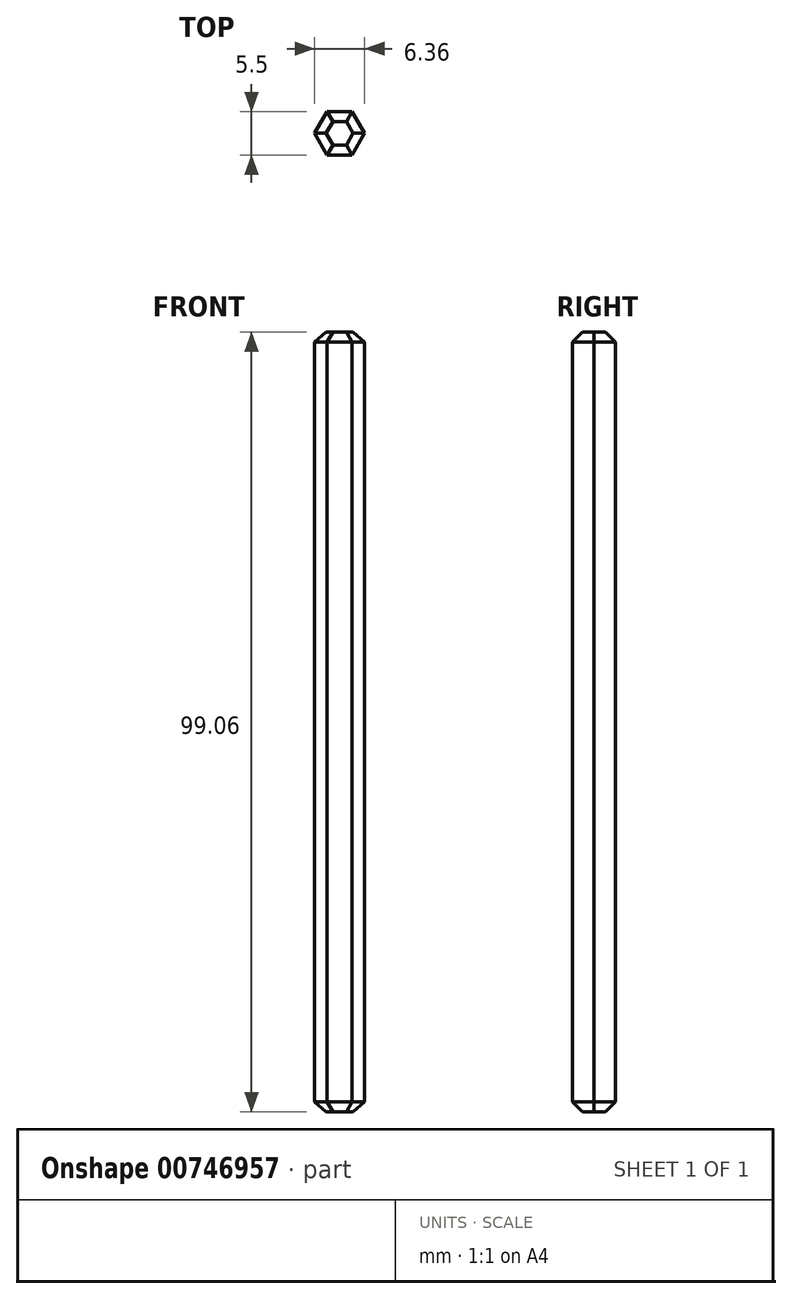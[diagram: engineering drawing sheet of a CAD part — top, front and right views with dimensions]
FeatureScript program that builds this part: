
annotation { "Feature Type Name" : "Feature", "Feature Type Description" : "" }
export const myFeature = defineFeature(function(context is Context, id is Id, definition is map)
    precondition{}
    {
        {
            var Q0;
            Q0=qCreatedBy(makeId("Top.planeOp"),FACE);
            var sketch = newSketch(context, id + "F0", { "sketchPlane" : qUnion([Q0])});
            skCircle(sketch, "E0.cCircle", {"center": v(0, 0) * mm, "radius": 3.18 * mm, "construction": true});
            skLineSegment(sketch, "E0.0", {"start": v(3.17, 0) * mm, "end": v(1.59, -2.75) * mm});
            skLineSegment(sketch, "E0.1", {"start": v(1.59, -2.75) * mm, "end": v(-1.59, -2.75) * mm});
            skLineSegment(sketch, "E0.2", {"start": v(-1.59, -2.75) * mm, "end": v(-3.17, 0) * mm});
            skLineSegment(sketch, "E0.3", {"start": v(-3.17, 0) * mm, "end": v(-1.59, 2.75) * mm});
            skLineSegment(sketch, "E0.4", {"start": v(-1.59, 2.75) * mm, "end": v(1.59, 2.75) * mm});
            skLineSegment(sketch, "E0.5", {"start": v(1.59, 2.75) * mm, "end": v(3.17, 0) * mm});
            skSolve(sketch);
        }
        {
            var Q0;
            Q0=makeQuery(id+"F0.imprint","IMPRINT",FACE,{"disambiguationData":[TD([[makeQuery(id+"F0.imprint","IMPRINT",EDGE,{"derivedFrom":sQuery(id+"F0.wireOp",EDGE,"E0.0")}),-1.0]])]});
            extrude(context, id + "F1", {"entities" : qUnion([Q0]), "depth" : 99.06 * mm, "offsetDistance" : 25.4 * mm});
        }
        {
            var Q0;
            Q0=makeQuery(id+"F1.opExtrude","CAP_FACE",FACE,{"disambiguationData":[OSD([sQuery(id+"F0.wireOp",EDGE,"E0.0"),sQuery(id+"F0.wireOp",EDGE,"E0.1"),sQuery(id+"F0.wireOp",EDGE,"E0.2"),sQuery(id+"F0.wireOp",EDGE,"E0.3"),sQuery(id+"F0.wireOp",EDGE,"E0.4"),sQuery(id+"F0.wireOp",EDGE,"E0.5")])],"isStart":false});
            chamfer(context, id + "F2", {"entities" : qUnion([Q0]), "width" : 1.27 * mm, "tangentPropagation" : true});
        }
        {
            var Q0;
            Q0=makeQuery(id+"F1.opExtrude","CAP_FACE",FACE,{"disambiguationData":[OSD([sQuery(id+"F0.wireOp",EDGE,"E0.0"),sQuery(id+"F0.wireOp",EDGE,"E0.1"),sQuery(id+"F0.wireOp",EDGE,"E0.2"),sQuery(id+"F0.wireOp",EDGE,"E0.3"),sQuery(id+"F0.wireOp",EDGE,"E0.4"),sQuery(id+"F0.wireOp",EDGE,"E0.5")])],"isStart":true});
            chamfer(context, id + "F3", {"entities" : qUnion([Q0]), "width" : 1.27 * mm, "tangentPropagation" : true});
        }
    });
